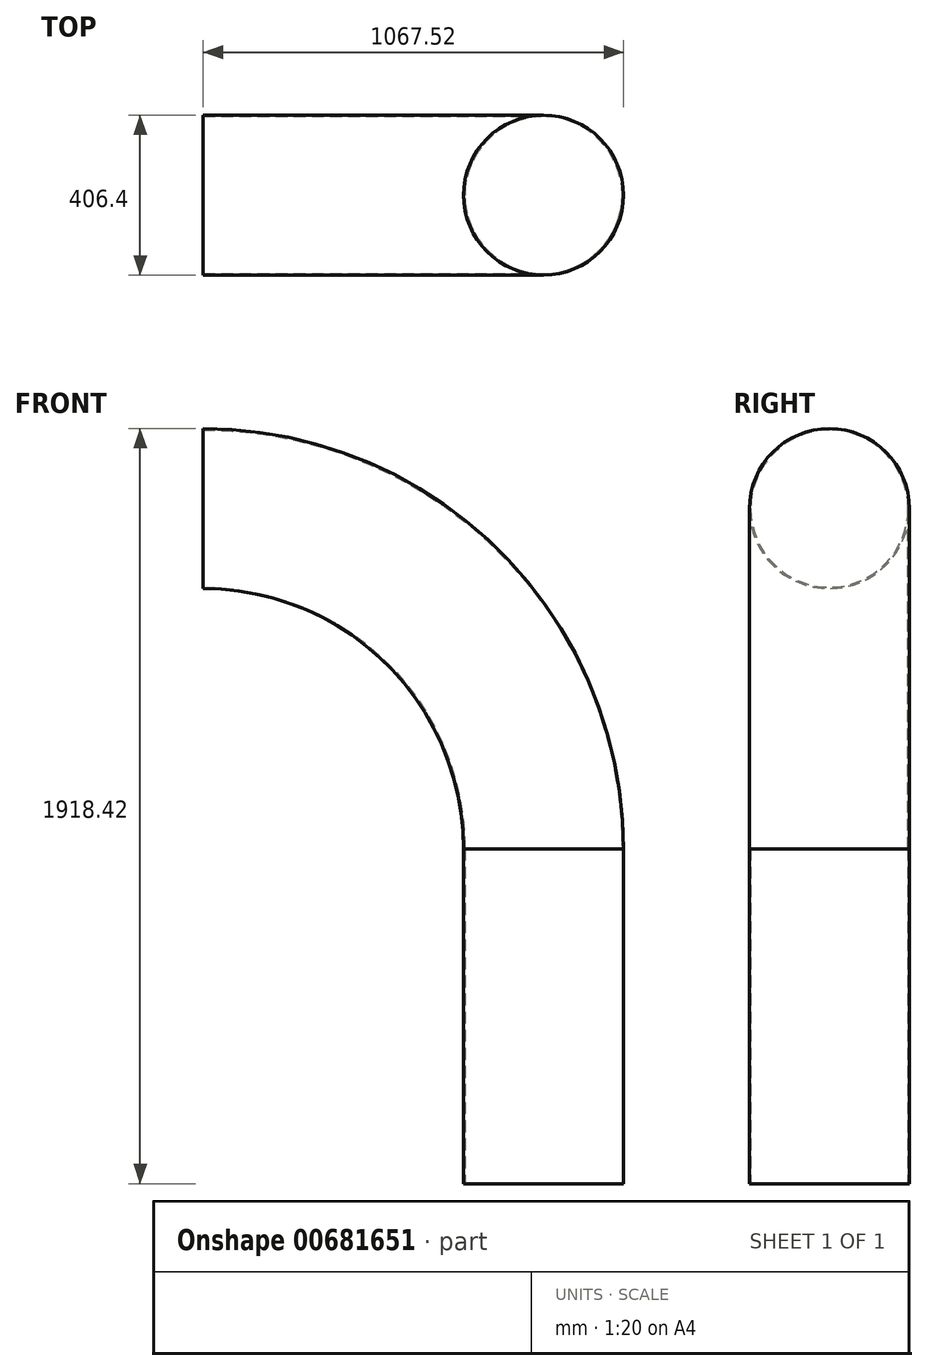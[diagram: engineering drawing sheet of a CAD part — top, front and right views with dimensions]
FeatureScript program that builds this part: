
annotation { "Feature Type Name" : "Feature", "Feature Type Description" : "" }
export const myFeature = defineFeature(function(context is Context, id is Id, definition is map)
    precondition{}
    {
        {
            var Q0;
            Q0=qCreatedBy(makeId("Front.planeOp"),FACE);
            var sketch = newSketch(context, id + "F0", { "sketchPlane" : qUnion([Q0])});
            skLineSegment(sketch, "E0", {"start": v(0, 0) * mm, "end": v(0, 850.9) * mm, "construction": true});
            skLineSegment(sketch, "E1", {"start": v(0, 850.9) * mm, "end": v(0, 1752.6) * mm, "construction": true});
            skLineSegment(sketch, "E2", {"start": v(0, 1752.6) * mm, "end": v(-863.6, 1752.6) * mm, "construction": true});
            skLineSegment(sketch, "E3", {"start": v(-863.6, 1752.6) * mm, "end": v(-863.6, 1549.4) * mm, "construction": true});
            skLineSegment(sketch, "E4", {"start": v(0, 0) * mm, "end": v(-203.2, 0) * mm, "construction": true});
            skLineSegment(sketch, "E5", {"start": v(0, 850.9) * mm, "end": v(-863.6, 850.9) * mm, "construction": true});
            skLineSegment(sketch, "E6", {"start": v(-863.6, 850.9) * mm, "end": v(-863.6, 1549.4) * mm, "construction": true});
            skSolve(sketch);
        }
        {
            var Q0;
            Q0=sQuery(id+"F0.wireOp",EDGE,"E5");
            cPlane(context, id + "F1", {"entities" : qUnion([Q0]), "cplaneType" : CPlaneType.LINE_ANGLE, "offset" : 25.4 * mm, "angle" : 90 * degree, "width" : 152.4 * mm, "height" : 152.4 * mm});
        }
        {
            var Q0;
            Q0=qCreatedBy(id+"F1.planeOp",FACE);
            var sketch = newSketch(context, id + "F2", { "sketchPlane" : qUnion([Q0])});
            skCircle(sketch, "E7", {"center": v(0, 0) * mm, "radius": 203.2 * mm});
            skLineSegment(sketch, "E8", {"start": v(-864.32, 0) * mm, "end": v(-723.29, 0) * mm, "construction": true});
            skLineSegment(sketch, "E9", {"start": v(-864.32, 0) * mm, "end": v(-864.32, -178.22) * mm, "construction": true});
            skSolve(sketch);
        }
        {
            var Q0;
            Q0 = qSketchRegion(id + "F2", true);
            var Q1;
            Q1=sQuery(id+"F2.wireOp",EDGE,"E9");
            revolve(context, id + "F3", {"surfaceOperationType" : NewSurfaceOperationType.NEW, "entities" : qUnion([Q0]), "axis" : qUnion([Q1]), "revolveType" : RevolveType.ONE_DIRECTION, "angle" : 90 * degree});
        }
        {
            var Q0;
            Q0=makeQuery(id+"F3.opRevolve","CAP_FACE",FACE,{"disambiguationData":[OSD([sQuery(id+"F2.wireOp",EDGE,"E7")])],"isStart":false});
            var Q1;
            Q1=makeQuery(id+"F3.opRevolve","CAP_FACE",FACE,{"disambiguationData":[OSD([sQuery(id+"F2.wireOp",EDGE,"E7")])],"isStart":true});
            shell(context, id + "F4", {"entities" : qUnion([Q0, Q1]), "thickness" : 3.17 * mm});
        }
        {
            var Q0;
            Q0=qCreatedBy(makeId("Top.planeOp"),FACE);
            var sketch = newSketch(context, id + "F5", { "sketchPlane" : qUnion([Q0])});
            skCircle(sketch, "E10", {"center": v(0, 0) * mm, "radius": 203.2 * mm});
            skCircle(sketch, "E11", {"center": v(0, 0) * mm, "radius": 200.03 * mm});
            skSolve(sketch);
        }
        {
            var Q0;
            Q0=makeQuery(id+"F5.imprint","IMPRINT",FACE,{"disambiguationData":[TD([[makeQuery(id+"F5.imprint","IMPRINT",EDGE,{"derivedFrom":sQuery(id+"F5.wireOp",EDGE,"E10")}),1.0]])]});
            extrude(context, id + "F6", {"entities" : qUnion([Q0]), "depth" : 850.9 * mm, "offsetDistance" : 25.4 * mm});
        }
    });
